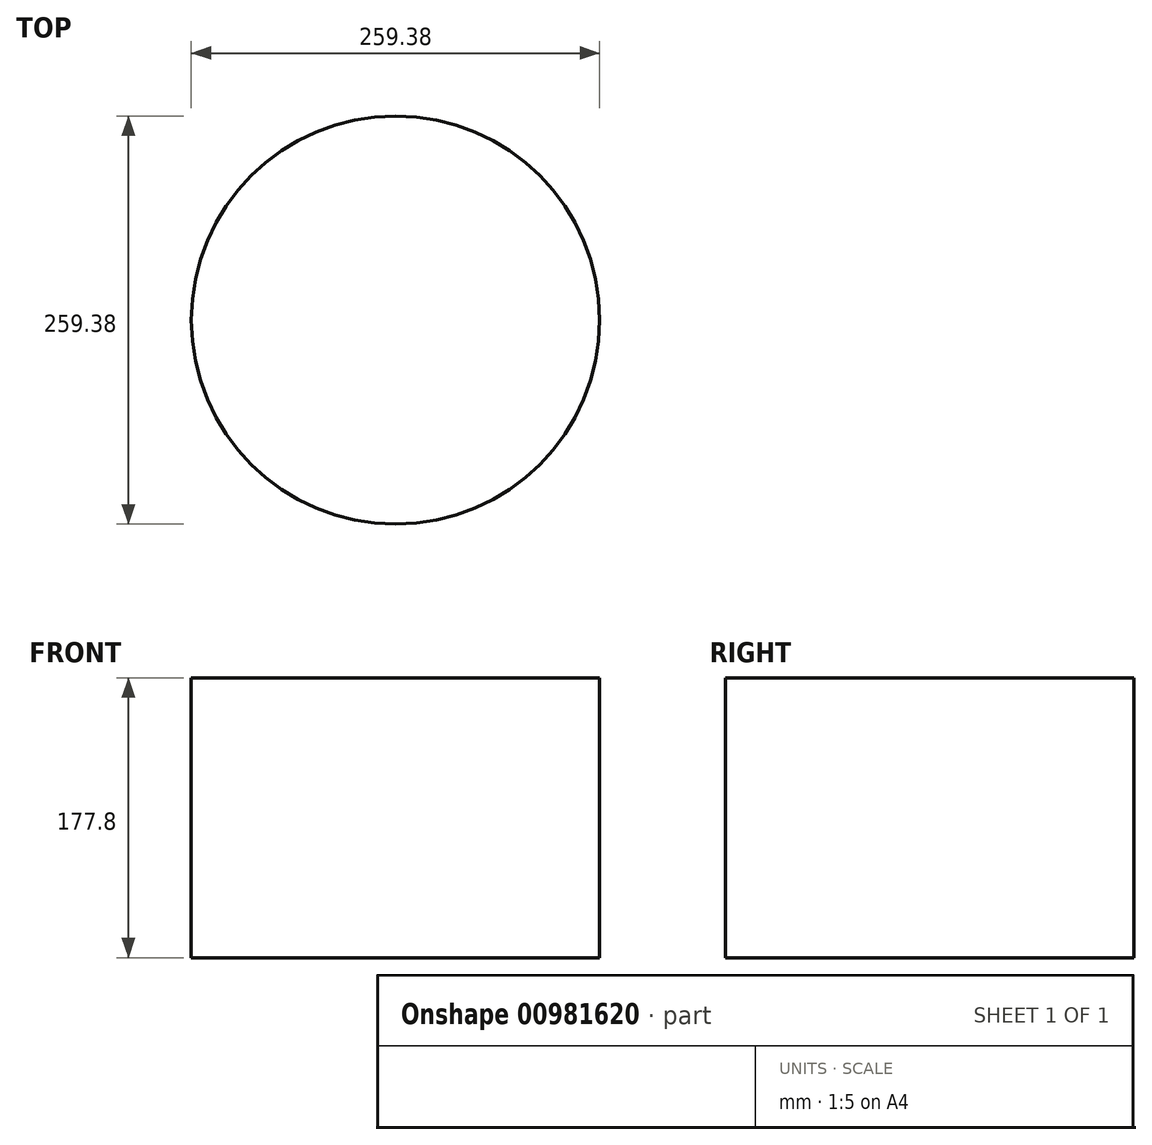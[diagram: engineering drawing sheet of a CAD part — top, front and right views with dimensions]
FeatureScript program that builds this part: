
annotation { "Feature Type Name" : "Feature", "Feature Type Description" : "" }
export const myFeature = defineFeature(function(context is Context, id is Id, definition is map)
    precondition{}
    {
        {
            var Q0;
            Q0=qCreatedBy(makeId("Top.planeOp"),FACE);
            var sketch = newSketch(context, id + "F0", { "sketchPlane" : qUnion([Q0])});
            skCircle(sketch, "E0", {"center": v(0, 0) * mm, "radius": 129.69 * mm});
            skSolve(sketch);
        }
        {
            var Q0;
            Q0=sQuery(id+"F0.wireOp",EDGE,"E0");
            extrude(context, id + "F1", {"bodyType" : ToolBodyType.SURFACE, "surfaceEntities" : qUnion([Q0]), "depth" : 177.8 * mm, "offsetDistance" : 25.4 * mm});
        }
    });
